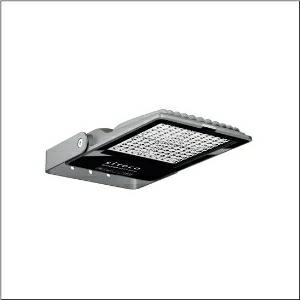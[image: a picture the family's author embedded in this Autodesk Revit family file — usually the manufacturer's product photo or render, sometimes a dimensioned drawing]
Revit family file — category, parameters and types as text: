
# Revit family: sicompact_r__31_mini___pl32_5xa7571c2k23_606d
name_source: partatom
category: Lighting Fixtures
units: mm (PartAtom-declared; Revit-internal decimal feet)

## family parameters
Cut with Voids When Loaded = No
Host = Face
Light Source = No
Part Type = Normal
Room Calculation Point = No
Round Connector Dimension = Use Diameter
Shared = No

## types (1)
- SiCompact® 31 mini  PL32 (1 x LED, 15000 lm, 95 W, 4000K)
    Apparent Load = 95 VA
    CIE Flux Codes = 32 69 98 100 100
    Color Rendering = 70
    Color Temperature = 4000K
    Default Elevation = 1800 mm
    Description = SiCompact® 31 mini, floodlight, primary light control with lens, of plastic, of toughened safety glass, transparent, light distribution: PL32, light emission: direct distribution, primary light characteristic: asymmetric, installation type: surface-mounted, LED, High Power LED, rated luminous flux: 15.000lm, luminous efficacy: 158lm/W, light colour: 740, colour temperature: 4000K, control gear: ON/OFF, with cable, 3x 1.5mm², mains connection: 220..240V, AC, 50/60Hz, connection cable pre-assembled, cable length: 2m, rated input power: 95W, of diecast aluminium, specular, metallic grey (RAL 9006), length: 461mm, width: 261mm, height: 62mm, bracket, of sheet steel, coated, metallic grey (RAL 9006), ON/OFF, protection rating (complete): IP66, insulation class (complete): insulation class I (protective earthing), certification: CE, ENEC, impact resistance: IK08, permissible operating ambient temperature: -40..+45°C, packaging unit: 1 piece

Light Distribution: PL32
    Height = 62 mm  [stored 0.203412 ft]
    Lamp = 1 x LED
    Lamp Light Flux = 15000 lm
    Lamp Power = 95 W
    Lamp count = 1
    Length = 460 mm
    Luminous efficacy = 158 lm/W
    Manufacturer = Siteco
    ModVariant = No
    Model = 5XA7571C2K23
    Mounting Place = Wall
    Mounting Type = Surface mounted
    Number of Poles = 1
    OnlyDefault = Yes
    Power Factor = 1
    Product Name = SiCompact® 31 mini | PL32
    Product group = floodlight | wall mounted
    ProductGroupID = 2001
    Protection Class = Protection class I
    Protection Degree = IP 66
    RLX_Detail_Level = 1
    RLX_Emergency_Light_Flux = 0 lm
    RLX_Emergency_Type = 0
    RLX_Emergency_Type_DB = No
    RlxData = <blob elided: 126633 chars, md5=600868a3>
    Socket = socket
    Standby Power = 0 W
    System Light Flux = 15000 lm
    System Power = 95 W
    Type Comments = Product without accessories
    Type Image = l_1006951.jpg
    URL = http://relux.com
    VarID = ---
    Voltage = 0 V
    Weight = 0.00 kg
    Width = 260 mm

note: [stored X ft] marks values corroborated as IEEE doubles in the binary element streams (Revit-internal decimal feet)

## geometry (parser evidence)
native form markers: Blend x4, Sweep x16
no freeform markers — native parametric forms only
